# Revit family: JC KONTAKTER JCK117AT SV
name_source: partatom
category: Specialty Equipment
units: mm (PartAtom-declared; Revit-internal decimal feet)

## family parameters
Cut with Voids When Loaded = No
Enable Cutting in Views = Yes
Host = Face
Maintain Annotation Orientation = Yes
Part Type = Normal
Room Calculation Point = No
Round Connector Dimension = Use Diameter
Shared = No

## types (1)
- JCK117AT
    Antal mikrobrytare = 2
    CE Dokument = https://jckontakter.se
    Default Elevation = 800 mm  [stored 2.62467 ft]
    Description = Stilren, robust armbågskontakt med plan tryckplatta i rostfri metall och underdel i silvereloxerad aluminium. Modellen är utvecklad för att användas i exklusiva miljöer och i äldre, k-märkta byggnader.

Kan med fördel göras trådlös genom tillval, då det ofta är svårt att dra kablage i äldre byggnader.
    Endcap = Plast
    Lock = Rostfrit Stål
    Lägsta märkström = 1mA/4 V DC
    Manufacturer = JC Kontakter
    Mikrobrytare = Standard NO IP67
    Model = JCK117AT
    Nominell märkström = 12 V - Resistive 6A Inductive L/R 5ms 6A, 24 V - Resistive 6A Inductive L/R 5ms 5A
    Placering av armbågskontakt = https://jckontakter.se
    Power factor = 1
    Produktvikt = 0.410 kg
    Tekniskt produktblad = https://jckontakter.se
    Tillvalsförteckning = https://jckontakter.se
    Tillverkningsland = Sverige
    URL = https://jckontakter.se
    Underdel = Aluminum ENAW 6060
    Voltage = 24 V

note: [stored X ft] marks values corroborated as IEEE doubles in the binary element streams (Revit-internal decimal feet)

## geometry (parser evidence)
native form markers: Sweep x5
no freeform markers — native parametric forms only
